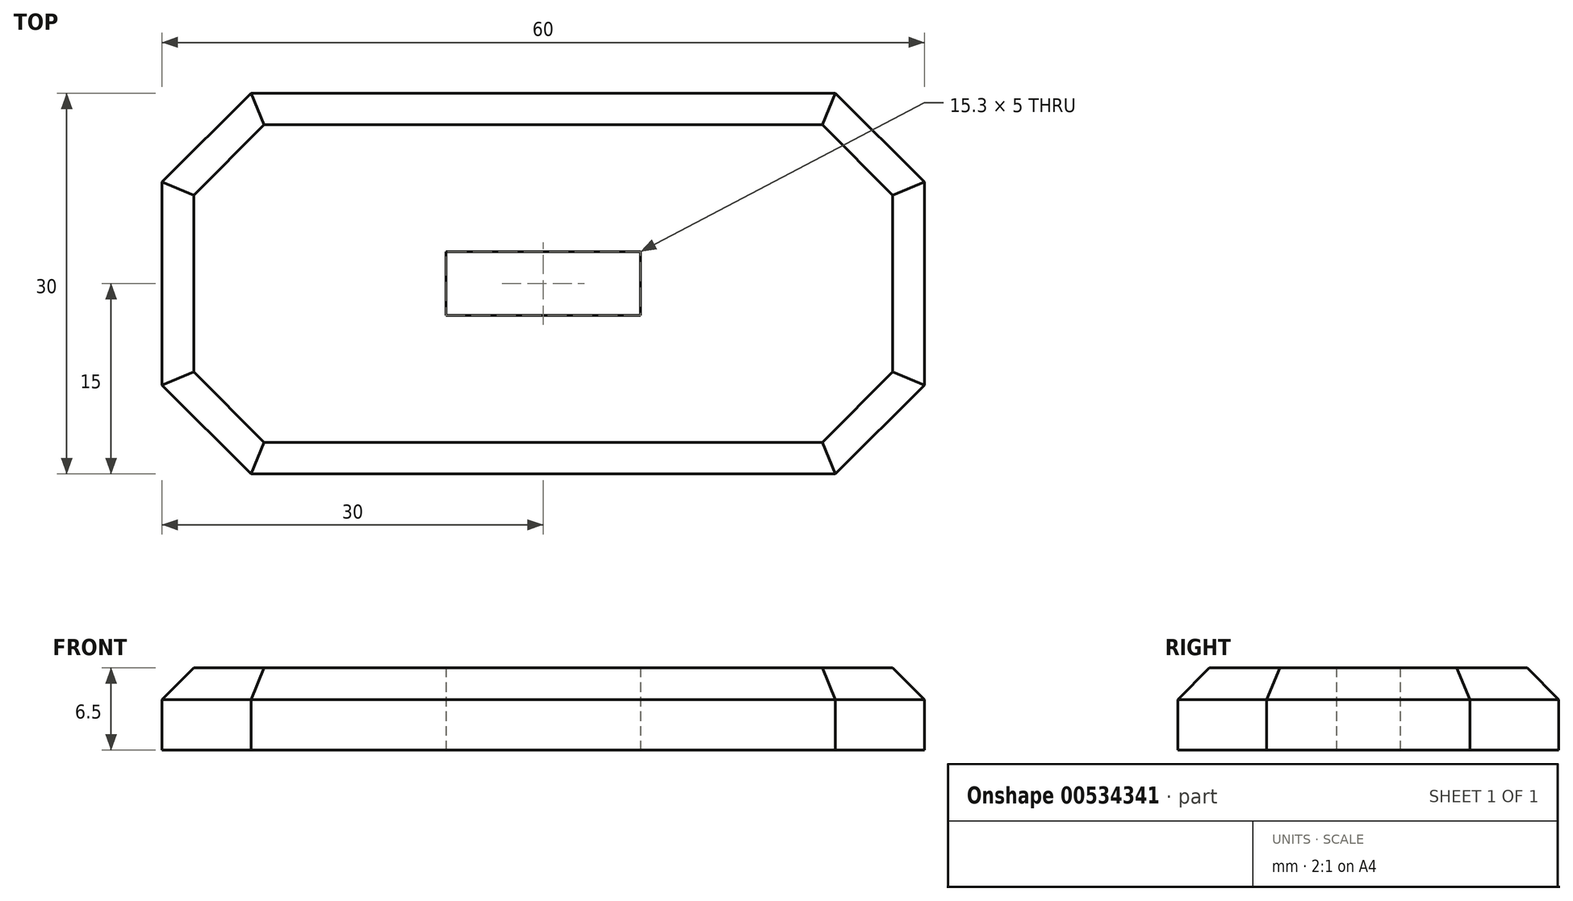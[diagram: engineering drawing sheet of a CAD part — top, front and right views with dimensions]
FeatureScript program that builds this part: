
annotation { "Feature Type Name" : "Feature", "Feature Type Description" : "" }
export const myFeature = defineFeature(function(context is Context, id is Id, definition is map)
    precondition{}
    {
        {
            var Q0;
            Q0=qCreatedBy(makeId("Top.planeOp"),FACE);
            var sketch = newSketch(context, id + "F0", { "sketchPlane" : qUnion([Q0])});
            skLineSegment(sketch, "E0.bottom", {"start": v(30, -15) * mm, "end": v(-30, -15) * mm});
            skLineSegment(sketch, "E0.top", {"start": v(30, 15) * mm, "end": v(-30, 15) * mm});
            skLineSegment(sketch, "E0.left", {"start": v(30, -15) * mm, "end": v(30, 15) * mm});
            skLineSegment(sketch, "E0.right", {"start": v(-30, -15) * mm, "end": v(-30, 15) * mm});
            skPoint(sketch, "E0.middle", {"position": v(0, 0) * mm});
            skLineSegment(sketch, "E1.bottom", {"start": v(7.65, -2.5) * mm, "end": v(-7.65, -2.5) * mm});
            skLineSegment(sketch, "E1.top", {"start": v(7.65, 2.5) * mm, "end": v(-7.65, 2.5) * mm});
            skLineSegment(sketch, "E1.left", {"start": v(7.65, -2.5) * mm, "end": v(7.65, 2.5) * mm});
            skLineSegment(sketch, "E1.right", {"start": v(-7.65, -2.5) * mm, "end": v(-7.65, 2.5) * mm});
            skSolve(sketch);
        }
        {
            var Q0;
            Q0=makeQuery(id+"F0.imprint","IMPRINT",FACE,{"disambiguationData":[TD([[makeQuery(id+"F0.imprint","IMPRINT",EDGE,{"derivedFrom":sQuery(id+"F0.wireOp",EDGE,"E0.bottom")}),-1.0]])]});
            extrude(context, id + "F1", {"entities" : qUnion([Q0]), "depth" : 6.5 * mm, "offsetDistance" : 25 * mm});
        }
        {
            var Q0;
            Q0=makeQuery(id+"F1.opExtrude","SWEPT_EDGE",EDGE,{"disambiguationData":[OSD([sQuery(id+"F0.wireOp",EDGE,"E0.bottom"),sQuery(id+"F0.wireOp",EDGE,"E0.right")])]});
            var Q1;
            Q1=makeQuery(id+"F1.opExtrude","SWEPT_EDGE",EDGE,{"disambiguationData":[OSD([sQuery(id+"F0.wireOp",EDGE,"E0.bottom"),sQuery(id+"F0.wireOp",EDGE,"E0.left")])]});
            var Q2;
            Q2=makeQuery(id+"F1.opExtrude","SWEPT_EDGE",EDGE,{"disambiguationData":[OSD([sQuery(id+"F0.wireOp",EDGE,"E0.top"),sQuery(id+"F0.wireOp",EDGE,"E0.left")])]});
            var Q3;
            Q3=makeQuery(id+"F1.opExtrude","SWEPT_EDGE",EDGE,{"disambiguationData":[OSD([sQuery(id+"F0.wireOp",EDGE,"E0.top"),sQuery(id+"F0.wireOp",EDGE,"E0.right")])]});
            chamfer(context, id + "F2", {"entities" : qUnion([Q0, Q1, Q2, Q3]), "width" : 7 * mm, "tangentPropagation" : true});
        }
        {
            var Q0;
            Q0=makeQuery(id+"F1.opExtrude","CAP_EDGE",EDGE,{"disambiguationData":[OSD([sQuery(id+"F0.wireOp",EDGE,"E0.top")])],"isStart":false});
            var Q1;
            {var subQ0=sQuery(id+"F0.wireOp",EDGE,"E0.right");var subQ1=sQuery(id+"F0.wireOp",EDGE,"E0.top");Q1=makeQuery(id+"F2.opChamfer","BLEND_EDGE",EDGE,{"blendedFrom":[makeQuery(id+"F1.opExtrude","SWEPT_EDGE",EDGE,{"disambiguationData":[OSD([subQ1,subQ0])]}),makeQuery(id+"F1.opExtrude","CAP_FACE",FACE,{"disambiguationData":[OSD([sQuery(id+"F0.wireOp",EDGE,"E0.bottom"),subQ1,sQuery(id+"F0.wireOp",EDGE,"E0.left"),subQ0,sQuery(id+"F0.wireOp",EDGE,"E1.bottom"),sQuery(id+"F0.wireOp",EDGE,"E1.top"),sQuery(id+"F0.wireOp",EDGE,"E1.left"),sQuery(id+"F0.wireOp",EDGE,"E1.right")])],"isStart":false})],"blendedInto":[makeQuery(id+"F1.opExtrude","CAP_FACE",FACE,{"disambiguationData":[OSD([sQuery(id+"F0.wireOp",EDGE,"E0.bottom"),subQ1,sQuery(id+"F0.wireOp",EDGE,"E0.left"),subQ0,sQuery(id+"F0.wireOp",EDGE,"E1.bottom"),sQuery(id+"F0.wireOp",EDGE,"E1.top"),sQuery(id+"F0.wireOp",EDGE,"E1.left"),sQuery(id+"F0.wireOp",EDGE,"E1.right")])],"isStart":false})]});}
            var Q2;
            Q2=makeQuery(id+"F1.opExtrude","CAP_EDGE",EDGE,{"disambiguationData":[OSD([sQuery(id+"F0.wireOp",EDGE,"E0.right")])],"isStart":false});
            var Q3;
            {var subQ0=sQuery(id+"F0.wireOp",EDGE,"E0.right");var subQ1=sQuery(id+"F0.wireOp",EDGE,"E0.bottom");Q3=makeQuery(id+"F2.opChamfer","BLEND_EDGE",EDGE,{"blendedFrom":[makeQuery(id+"F1.opExtrude","SWEPT_EDGE",EDGE,{"disambiguationData":[OSD([subQ1,subQ0])]}),makeQuery(id+"F1.opExtrude","CAP_FACE",FACE,{"disambiguationData":[OSD([subQ1,sQuery(id+"F0.wireOp",EDGE,"E0.top"),sQuery(id+"F0.wireOp",EDGE,"E0.left"),subQ0,sQuery(id+"F0.wireOp",EDGE,"E1.bottom"),sQuery(id+"F0.wireOp",EDGE,"E1.top"),sQuery(id+"F0.wireOp",EDGE,"E1.left"),sQuery(id+"F0.wireOp",EDGE,"E1.right")])],"isStart":false})],"blendedInto":[makeQuery(id+"F1.opExtrude","CAP_FACE",FACE,{"disambiguationData":[OSD([subQ1,sQuery(id+"F0.wireOp",EDGE,"E0.top"),sQuery(id+"F0.wireOp",EDGE,"E0.left"),subQ0,sQuery(id+"F0.wireOp",EDGE,"E1.bottom"),sQuery(id+"F0.wireOp",EDGE,"E1.top"),sQuery(id+"F0.wireOp",EDGE,"E1.left"),sQuery(id+"F0.wireOp",EDGE,"E1.right")])],"isStart":false})]});}
            var Q4;
            Q4=makeQuery(id+"F1.opExtrude","CAP_EDGE",EDGE,{"disambiguationData":[OSD([sQuery(id+"F0.wireOp",EDGE,"E0.bottom")])],"isStart":false});
            var Q5;
            {var subQ0=sQuery(id+"F0.wireOp",EDGE,"E0.left");var subQ1=sQuery(id+"F0.wireOp",EDGE,"E0.bottom");Q5=makeQuery(id+"F2.opChamfer","BLEND_EDGE",EDGE,{"blendedFrom":[makeQuery(id+"F1.opExtrude","SWEPT_EDGE",EDGE,{"disambiguationData":[OSD([subQ1,subQ0])]}),makeQuery(id+"F1.opExtrude","CAP_FACE",FACE,{"disambiguationData":[OSD([subQ1,sQuery(id+"F0.wireOp",EDGE,"E0.top"),subQ0,sQuery(id+"F0.wireOp",EDGE,"E0.right"),sQuery(id+"F0.wireOp",EDGE,"E1.bottom"),sQuery(id+"F0.wireOp",EDGE,"E1.top"),sQuery(id+"F0.wireOp",EDGE,"E1.left"),sQuery(id+"F0.wireOp",EDGE,"E1.right")])],"isStart":false})],"blendedInto":[makeQuery(id+"F1.opExtrude","CAP_FACE",FACE,{"disambiguationData":[OSD([subQ1,sQuery(id+"F0.wireOp",EDGE,"E0.top"),subQ0,sQuery(id+"F0.wireOp",EDGE,"E0.right"),sQuery(id+"F0.wireOp",EDGE,"E1.bottom"),sQuery(id+"F0.wireOp",EDGE,"E1.top"),sQuery(id+"F0.wireOp",EDGE,"E1.left"),sQuery(id+"F0.wireOp",EDGE,"E1.right")])],"isStart":false})]});}
            var Q6;
            Q6=makeQuery(id+"F1.opExtrude","CAP_EDGE",EDGE,{"disambiguationData":[OSD([sQuery(id+"F0.wireOp",EDGE,"E0.left")])],"isStart":false});
            var Q7;
            {var subQ0=sQuery(id+"F0.wireOp",EDGE,"E0.left");var subQ1=sQuery(id+"F0.wireOp",EDGE,"E0.top");Q7=makeQuery(id+"F2.opChamfer","BLEND_EDGE",EDGE,{"blendedFrom":[makeQuery(id+"F1.opExtrude","SWEPT_EDGE",EDGE,{"disambiguationData":[OSD([subQ1,subQ0])]}),makeQuery(id+"F1.opExtrude","CAP_FACE",FACE,{"disambiguationData":[OSD([sQuery(id+"F0.wireOp",EDGE,"E0.bottom"),subQ1,subQ0,sQuery(id+"F0.wireOp",EDGE,"E0.right"),sQuery(id+"F0.wireOp",EDGE,"E1.bottom"),sQuery(id+"F0.wireOp",EDGE,"E1.top"),sQuery(id+"F0.wireOp",EDGE,"E1.left"),sQuery(id+"F0.wireOp",EDGE,"E1.right")])],"isStart":false})],"blendedInto":[makeQuery(id+"F1.opExtrude","CAP_FACE",FACE,{"disambiguationData":[OSD([sQuery(id+"F0.wireOp",EDGE,"E0.bottom"),subQ1,subQ0,sQuery(id+"F0.wireOp",EDGE,"E0.right"),sQuery(id+"F0.wireOp",EDGE,"E1.bottom"),sQuery(id+"F0.wireOp",EDGE,"E1.top"),sQuery(id+"F0.wireOp",EDGE,"E1.left"),sQuery(id+"F0.wireOp",EDGE,"E1.right")])],"isStart":false})]});}
            chamfer(context, id + "F3", {"entities" : qUnion([Q0, Q1, Q2, Q3, Q4, Q5, Q6, Q7]), "width" : 2.5 * mm, "tangentPropagation" : true});
        }
    });
